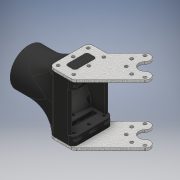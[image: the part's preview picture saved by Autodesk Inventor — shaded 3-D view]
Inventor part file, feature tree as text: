
AUTODESK INVENTOR PART (.ipt)
format: ipt  version: 2019 (Build 230136000, 136)  size: 1,574,400 bytes
history: native  units: mm
features: extrude x14, sketch x9, fillet x7, projected_geometry x5, plane x3, mirror x3, other x2, pattern_linear x1, pattern_circular x1, emboss x1
ambient origin geometry x8: Origin, YZ Plane, XZ Plane, XY Plane, X Axis, Y Axis, Z Axis, Center Point
bodies: Body1 (feature_tree), Body2 (feature_tree)
feature tree (46):
  other  "Aluminum PLates"
  plane  "Work Plane12"
  extrude  "Extrusion2"  Depth=2.0mm
  fillet  "Fillet7"  Radius=2.8mm
  extrude  "Extrusion15"  Depth=2.8mm
  sketch  "Sketch21"  dims[d46=2.8mm d47=2.8mm]
  extrude  "Extrusion17"  Depth=2.8mm
  extrude  "Extrusion18"  Depth=2.8mm
  extrude  "Extrusion19"  Depth=20.0mm
  extrude  "Extrusion20"  Depth=2.5mm
  fillet  "Fillet9"  Radius=2.5mm
  plane  "Work Plane14"
  extrude  "Extrusion22"  Depth=2.5mm
  extrude  "Extrusion21"  Depth=4.0mm TaperAngle=0.0deg
  pattern_linear  "Rectangular Pattern1"  Spacing1=4.5mm  [1 undecoded]
  plane  "Work Plane15"
  mirror  "Mirror4"
  mirror  "Mirror2"
  mirror  "Mirror5"
  extrude  "Extrusion25"  Depth=1.0mm
  extrude  "Extrusion23"  Depth=1.0mm
  fillet  "Fillet10"  Radius=4.5mm
  extrude  "Extrusion24"  Depth=1.0mm
  fillet  "Fillet12"  Radius=4.5mm
  pattern_circular  "Circular Pattern1"  [2 undecoded]
  extrude  "Extrusion26"  Depth=1.0mm
  sketch  "Sketch28"  dims[d140=23.5mm d144=4.0mm d145=0.0mm]
  extrude  "Extrusion27"  Depth=6.0mm TaperAngle=0.0deg
  emboss  "Emboss1"
  fillet  "Fillet11"  Radius=31.0mm
  extrude  "Extrusion28"  Depth=1.0mm TaperAngle=0.0deg
  fillet  "Fillet13"  Radius=4.0mm
  fillet  "Fillet14"  Radius=4.0mm
  sketch  "Sketch2"  dims[d17=2.0mm d18=0.0mm d42=2.8mm d43=2.8mm]
  sketch  "Sketch5"  dims[d44=2.8mm d45=2.8mm]
  other  "3D Printed Body"
  sketch  "Sketch23"  dims[d48=2.8mm d49=2.8mm]
  sketch  "Sketch24"  dims[d78=135.0deg d132=20.0mm]
  projected_geometry  "Projected Loop16"
  sketch  "Sketch26"  dims[d134=25.0mm d135=2.5mm d136=2.5mm]
  sketch  "Sketch27"  dims[d137=2.5mm d138=2.5mm]
  projected_geometry  "Projected Loop18"
  projected_geometry  "Projected Loop19"
  projected_geometry  "Projected Loop20"
  projected_geometry  "Projected Loop21"
  sketch  "Sketch29"  dims[d150=27.2mm d151=4.5mm d152=4.5mm d153=4.5mm d154=4.5mm d155=4.5mm d156=4.5mm d157=4.5mm d158=4.5mm d159=6.0mm d160=0.0mm d161=31.0mm d162=53.414mm d163=0.0mm d164=4.0mm d166=4.0mm d167=0.0mm d168=2.5mm d169=2.5mm d170=8.0mm d171=18.0mm d172=2.0mm d173=2.0mm d176=2.0mm d177=0.0mm d178=-4.0mm d183=1.8mm d184=0.0mm d185=30.0mm d187=12.5mm d188=2.0mm d189=0.0mm d191=30.0mm d193=33.0mm d194=15.0mm d195=0.0mm d196=7.0mm d197=22.876386mm d198=3.5mm d199=4.0mm d200=4.0mm d201=3.5mm d205=20.25mm d206=135.0deg d207=0.25mm d208=0.5mm d209=0.5mm d210=5.25mm d211=5.25mm d212=0.75mm d213=45.0deg d214=0.75mm d215=10.0mm d216=22.5deg d217=6.0mm d218=30.0mm d219=-0.523599mm d220=80.0mm d221=360.0deg d223=1.0mm d224=0.0mm d225=40.0mm d226=0.0mm d227=10.0mm d228=1.5mm d229=6.0mm d230=6.0mm d231=45.0mm d232=0.0mm d233=2.0mm d234=1.0mm d235=0.0mm d236=1.0mm d237=0.5mm d240=1.5mm d241=135.0deg d242=10.0mm d243=0.0mm d244=2.0mm d245=1.0mm]
note: 3 required parameter values undecoded (feature->parameter linkage not recoverable at this tier; creation-order binding heuristic only, values carry confidence <= 0.55)
